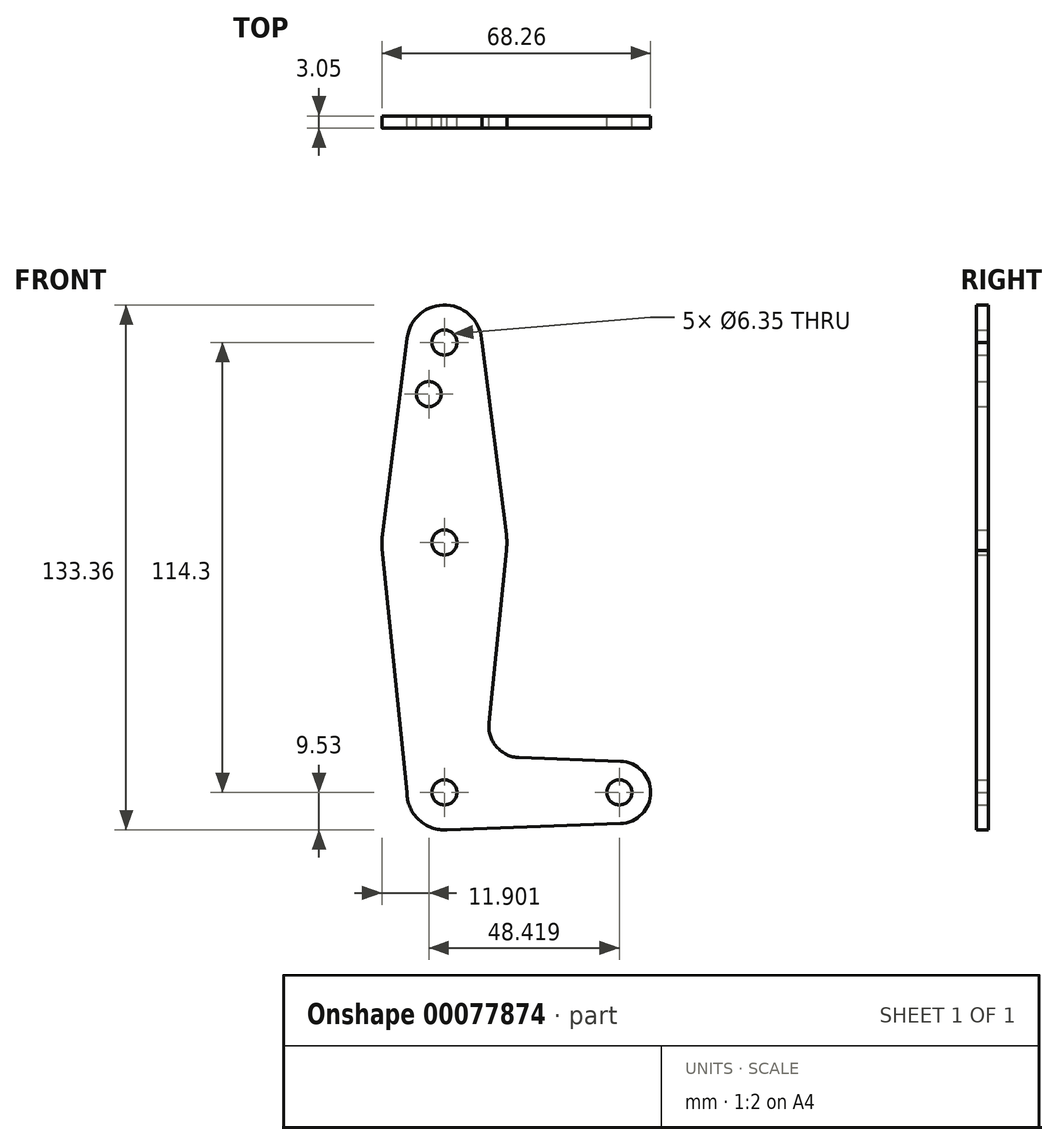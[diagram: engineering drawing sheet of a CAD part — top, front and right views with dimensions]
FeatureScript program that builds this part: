
annotation { "Feature Type Name" : "Feature", "Feature Type Description" : "" }
export const myFeature = defineFeature(function(context is Context, id is Id, definition is map)
    precondition{}
    {
        {
            var Q0;
            Q0=qCreatedBy(makeId("Front.planeOp"),FACE);
            cPlane(context, id + "F0", {"entities" : qUnion([Q0]), "cplaneType" : CPlaneType.OFFSET, "offset" : 152.4 * mm, "width" : 152.4 * mm, "height" : 152.4 * mm});
        }
        {
            var Q0;
            Q0=qCreatedBy(id+"F0.planeOp",FACE);
            var sketch = newSketch(context, id + "F1", { "sketchPlane" : qUnion([Q0])});
            skLineSegment(sketch, "E0", {"start": v(0, 0) * mm, "end": v(0, 114.3) * mm, "construction": true});
            skLineSegment(sketch, "E1", {"start": v(0, 63.5) * mm, "end": v(0, 114.3) * mm, "construction": true});
            skLineSegment(sketch, "E2", {"start": v(0, 0) * mm, "end": v(44.45, 0) * mm, "construction": true});
            skCircle(sketch, "E3", {"center": v(0, 114.3) * mm, "radius": 9.53 * mm});
            skCircle(sketch, "E4", {"center": v(0, 63.5) * mm, "radius": 15.88 * mm});
            skCircle(sketch, "E5", {"center": v(0, 0) * mm, "radius": 9.53 * mm});
            skCircle(sketch, "E6", {"center": v(44.45, 0) * mm, "radius": 7.94 * mm});
            skLineSegment(sketch, "E7", {"start": v(-9.45, 115.5) * mm, "end": v(-15.75, 65.48) * mm});
            skLineSegment(sketch, "E8", {"start": v(9.52, 114.3) * mm, "end": v(15.75, 65.5) * mm});
            skLineSegment(sketch, "E9", {"start": v(18.97, 8.85) * mm, "end": v(44.73, 7.93) * mm});
            skLineSegment(sketch, "E10", {"start": v(0, -9.53) * mm, "end": v(44.73, -7.93) * mm});
            skCircle(sketch, "E11", {"center": v(0, 114.3) * mm, "radius": 3.18 * mm});
            skCircle(sketch, "E12", {"center": v(0, 63.5) * mm, "radius": 3.18 * mm});
            skCircle(sketch, "E13", {"center": v(0, 0) * mm, "radius": 3.18 * mm});
            skCircle(sketch, "E14", {"center": v(44.45, 0) * mm, "radius": 3.18 * mm});
            skLineSegment(sketch, "E15", {"start": v(15.75, 61.5) * mm, "end": v(11.34, 17.59) * mm});
            skLineSegment(sketch, "E16", {"start": v(-9.52, 0) * mm, "end": v(-15.8, 61.9) * mm});
            skArc(sketch, "E17.filletArc", {"start": v(11.34, 17.59) * mm, "mid": v(13.26, 11.57) * mm, "end": v(18.97, 8.85) * mm});
            skCircle(sketch, "E18", {"center": v(-3.97, 101.2) * mm, "radius": 3.18 * mm});
            skSolve(sketch);
        }
        {
            var Q0;
            Q0 = qSketchRegion(id + "F1", true);
            extrude(context, id + "F2", {"entities" : qUnion([Q0]), "depth" : 3.05 * mm});
        }
    });
